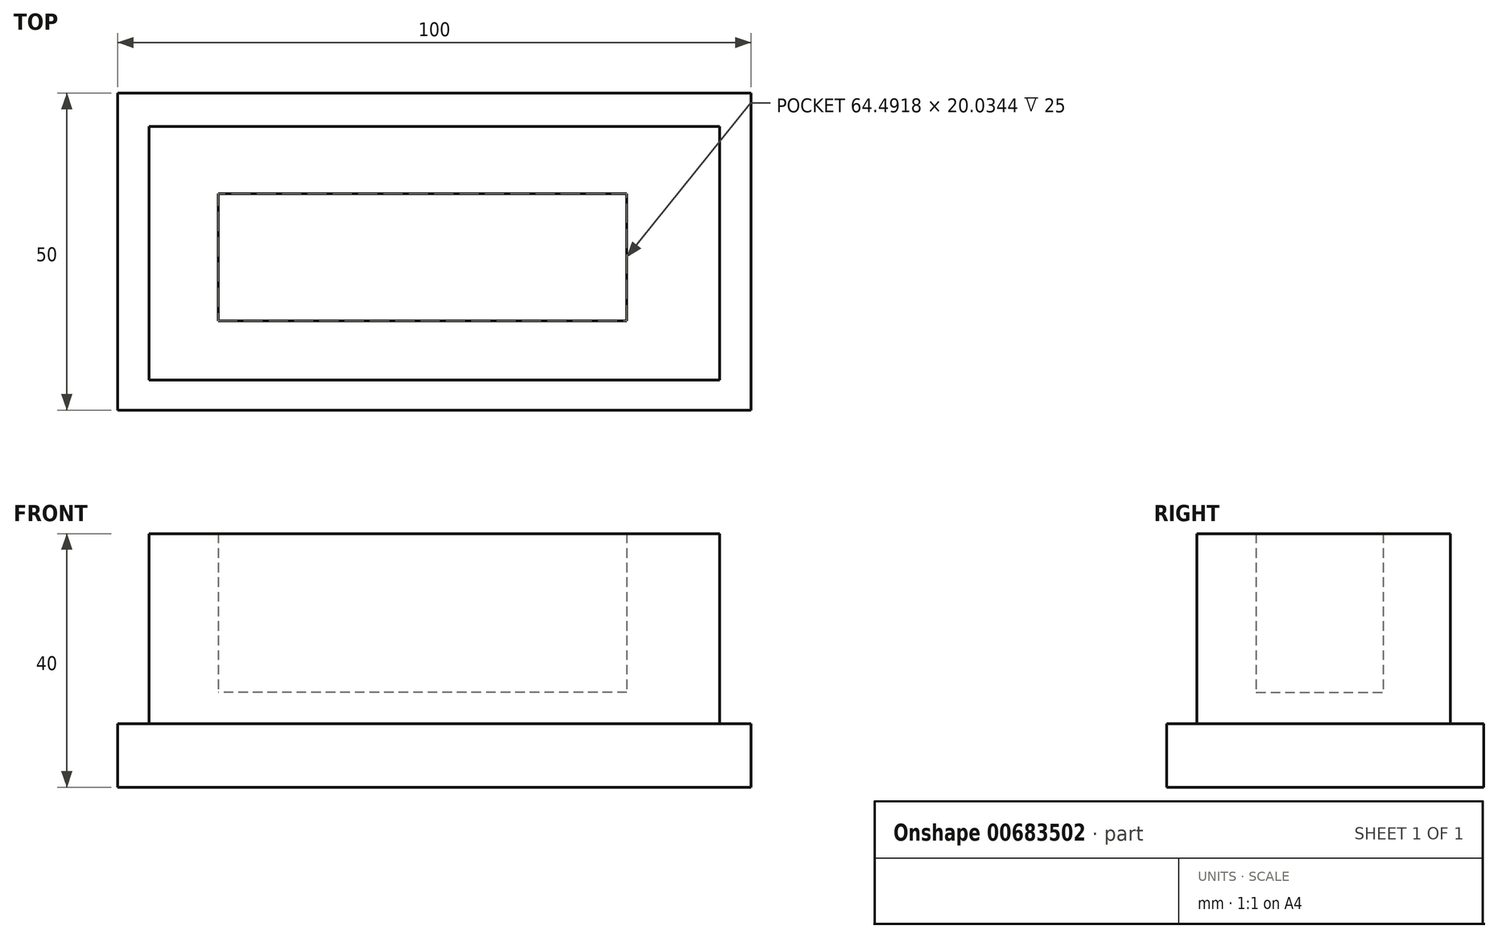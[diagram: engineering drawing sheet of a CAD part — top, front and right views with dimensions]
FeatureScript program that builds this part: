
annotation { "Feature Type Name" : "Feature", "Feature Type Description" : "" }
export const myFeature = defineFeature(function(context is Context, id is Id, definition is map)
    precondition{}
    {
        {
            var Q0;
            Q0=qCreatedBy(makeId("Top.planeOp"),FACE);
            var sketch = newSketch(context, id + "F0", { "sketchPlane" : qUnion([Q0])});
            skLineSegment(sketch, "E0.bottom", {"start": v(-52.13, 15.87) * mm, "end": v(47.87, 15.87) * mm});
            skLineSegment(sketch, "E0.top", {"start": v(-52.13, -34.13) * mm, "end": v(47.87, -34.13) * mm});
            skLineSegment(sketch, "E0.left", {"start": v(-52.13, 15.87) * mm, "end": v(-52.13, -34.13) * mm});
            skLineSegment(sketch, "E0.right", {"start": v(47.87, 15.87) * mm, "end": v(47.87, -34.13) * mm});
            skSolve(sketch);
        }
        {
            var Q0;
            Q0 = qSketchRegion(id + "F0", true);
            extrude(context, id + "F1", {"entities" : qUnion([Q0]), "depth" : 10 * mm, "offsetDistance" : 25 * mm});
        }
        {
            var Q0;
            Q0=makeQuery(id+"F1.opExtrude","CAP_FACE",FACE,{"disambiguationData":[OSD([sQuery(id+"F0.wireOp",EDGE,"E0.bottom"),sQuery(id+"F0.wireOp",EDGE,"E0.top"),sQuery(id+"F0.wireOp",EDGE,"E0.left"),sQuery(id+"F0.wireOp",EDGE,"E0.right")])],"isStart":false});
            var sketch = newSketch(context, id + "F2", { "sketchPlane" : qUnion([Q0])});
            skLineSegment(sketch, "E1.bottom", {"start": v(42.87, -29.37) * mm, "end": v(-47.13, -29.37) * mm});
            skLineSegment(sketch, "E1.top", {"start": v(42.87, 10.63) * mm, "end": v(-47.13, 10.63) * mm});
            skLineSegment(sketch, "E1.left", {"start": v(42.87, -29.37) * mm, "end": v(42.87, 10.63) * mm});
            skLineSegment(sketch, "E1.right", {"start": v(-47.13, -29.37) * mm, "end": v(-47.13, 10.63) * mm});
            skSolve(sketch);
        }
        {
            var Q0;
            Q0=makeQuery(id+"F2.imprint","IMPRINT",FACE,{"disambiguationData":[TD([[makeQuery(id+"F2.imprint","IMPRINT",EDGE,{"derivedFrom":sQuery(id+"F2.wireOp",EDGE,"E1.bottom")}),-1.0]])]});
            extrude(context, id + "F3", {"entities" : qUnion([Q0]), "operationType" : NewBodyOperationType.ADD, "depth" : 5 * mm, "offsetDistance" : 25 * mm});
        }
        {
            var Q0;
            Q0=makeQuery(id+"F3.opExtrude","CAP_FACE",FACE,{"disambiguationData":[OSD([sQuery(id+"F2.wireOp",EDGE,"E1.bottom"),sQuery(id+"F2.wireOp",EDGE,"E1.top"),sQuery(id+"F2.wireOp",EDGE,"E1.left"),sQuery(id+"F2.wireOp",EDGE,"E1.right")])],"isStart":false});
            var sketch = newSketch(context, id + "F4", { "sketchPlane" : qUnion([Q0])});
            skLineSegment(sketch, "E2.bottom", {"start": v(28.25, -20.03) * mm, "end": v(-36.25, -20.03) * mm});
            skLineSegment(sketch, "E2.top", {"start": v(28.25, 0) * mm, "end": v(-36.25, 0) * mm});
            skLineSegment(sketch, "E2.left", {"start": v(28.25, -20.03) * mm, "end": v(28.25, 0) * mm});
            skLineSegment(sketch, "E2.right", {"start": v(-36.25, -20.03) * mm, "end": v(-36.25, 0) * mm});
            skSolve(sketch);
        }
        {
            var Q0;
            Q0=makeQuery(id+"F4.imprint","IMPRINT",FACE,{"disambiguationData":[TD([[makeQuery(id+"F4.imprint","IMPRINT",EDGE,{"derivedFrom":sQuery(id+"F4.wireOp",EDGE,"E2.bottom")}),1.0]])]});
            extrude(context, id + "F5", {"entities" : qUnion([Q0]), "operationType" : NewBodyOperationType.ADD, "depth" : 25 * mm, "offsetDistance" : 25 * mm});
        }
    });
